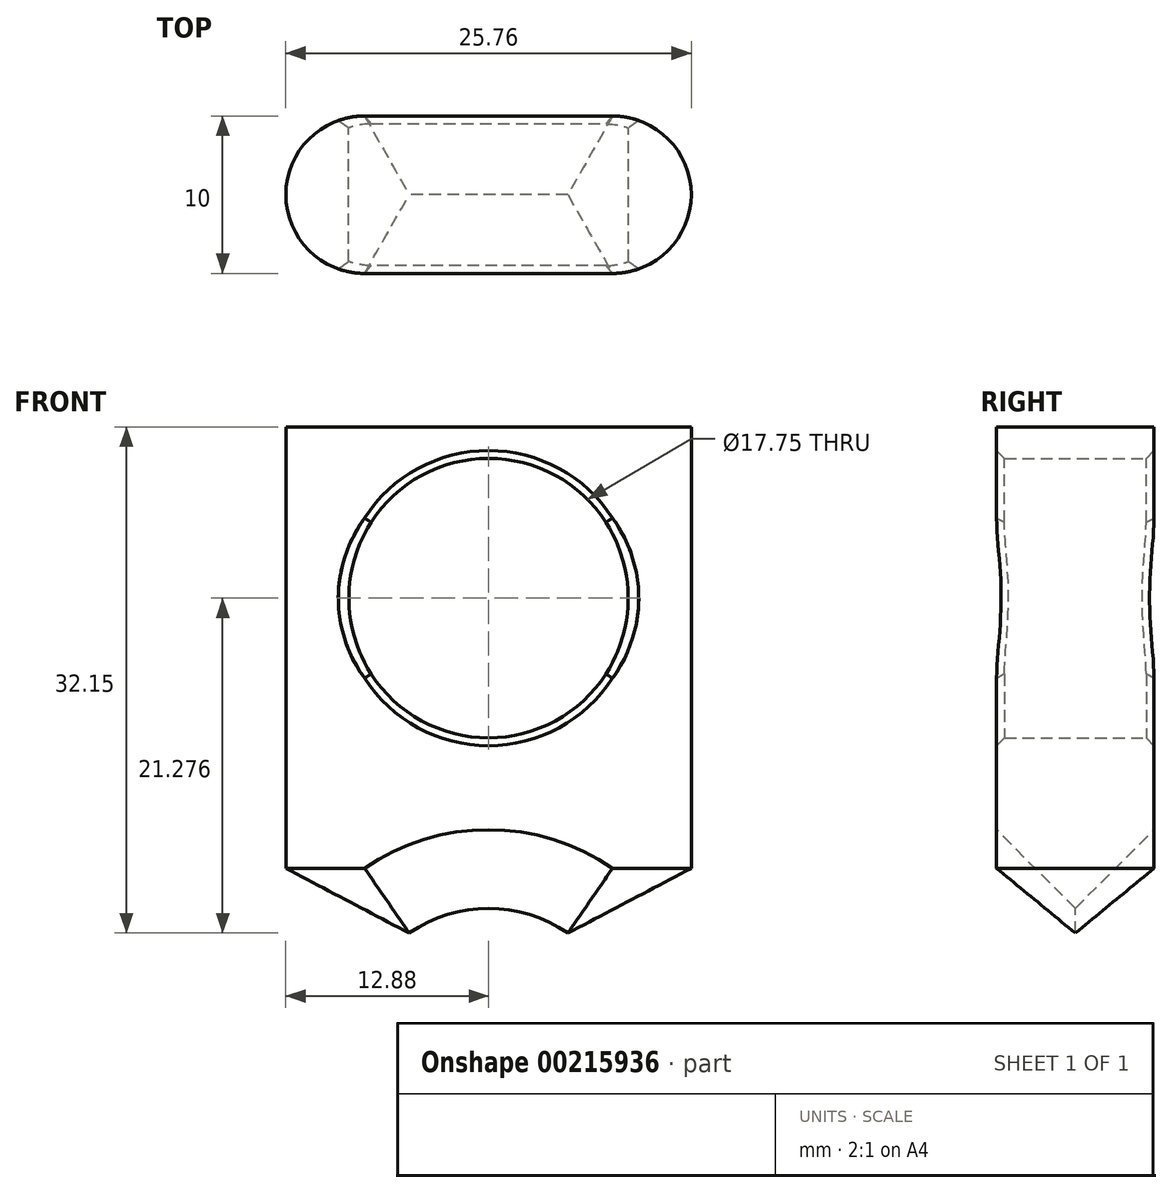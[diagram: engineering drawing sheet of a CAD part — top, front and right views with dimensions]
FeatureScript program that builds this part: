
annotation { "Feature Type Name" : "Feature", "Feature Type Description" : "" }
export const myFeature = defineFeature(function(context is Context, id is Id, definition is map)
    precondition{}
    {
        {
            var Q0;
            Q0=qCreatedBy(makeId("Front.planeOp"),FACE);
            var sketch = newSketch(context, id + "F0", { "sketchPlane" : qUnion([Q0])});
            skCircle(sketch, "E0", {"center": v(0, 0) * mm, "radius": 8.88 * mm});
            skLineSegment(sketch, "E1.bottom", {"start": v(-12.88, -10.54) * mm, "end": v(12.88, -10.54) * mm});
            skLineSegment(sketch, "E1.top", {"start": v(-12.88, 39.46) * mm, "end": v(12.87, 39.46) * mm});
            skLineSegment(sketch, "E1.left", {"start": v(-12.88, -10.54) * mm, "end": v(-12.88, 39.46) * mm});
            skLineSegment(sketch, "E1.right", {"start": v(12.88, -10.54) * mm, "end": v(12.87, 39.46) * mm});
            skCircle(sketch, "E2", {"center": v(0, 28.59) * mm, "radius": 8.88 * mm});
            skSolve(sketch);
        }
        {
            var Q0;
            Q0=makeQuery(id+"F0.imprint","IMPRINT",FACE,{"disambiguationData":[TD([[makeQuery(id+"F0.imprint","IMPRINT",EDGE,{"derivedFrom":sQuery(id+"F0.wireOp",EDGE,"E0")}),-1.0]])]});
            extrude(context, id + "F1", {"entities" : qUnion([Q0]), "depth" : 5 * mm, "hasSecondDirection" : true, "secondDirectionOppositeDirection" : true, "secondDirectionDepth" : 5 * mm});
        }
        {
            var Q0;
            Q0=makeQuery(id+"F1.opExtrude","CAP_EDGE",EDGE,{"disambiguationData":[OSD([sQuery(id+"F0.wireOp",EDGE,"E1.left")])],"isStart":false});
            var Q1;
            Q1=makeQuery(id+"F1.opExtrude","CAP_EDGE",EDGE,{"disambiguationData":[OSD([sQuery(id+"F0.wireOp",EDGE,"E1.left")])],"isStart":true});
            var Q2;
            Q2=makeQuery(id+"F1.opExtrude","CAP_EDGE",EDGE,{"disambiguationData":[OSD([sQuery(id+"F0.wireOp",EDGE,"E1.right")])],"isStart":false});
            var Q3;
            Q3=makeQuery(id+"F1.opExtrude","CAP_EDGE",EDGE,{"disambiguationData":[OSD([sQuery(id+"F0.wireOp",EDGE,"E1.right")])],"isStart":true});
            fillet(context, id + "F2", {"entities" : qUnion([Q0, Q1, Q2, Q3]), "radius" : 5 * mm, "tangentPropagation" : true, "allowEdgeOverflow" : false});
        }
        {
            var Q0;
            Q0=makeQuery(id+"F1.opExtrude","CAP_EDGE",EDGE,{"disambiguationData":[OSD([sQuery(id+"F0.wireOp",EDGE,"E0")])],"isStart":false});
            chamfer(context, id + "F3", {"entities" : qUnion([Q0]), "width" : 5 * mm, "tangentPropagation" : true});
        }
        {
            var Q0;
            Q0=makeQuery(id+"F0.imprint","IMPRINT",FACE,{"disambiguationData":[TD([[makeQuery(id+"F0.imprint","IMPRINT",EDGE,{"derivedFrom":sQuery(id+"F0.wireOp",EDGE,"E2")}),1.0]])]});
            extrude(context, id + "F4", {"entities" : qUnion([Q0]), "operationType" : NewBodyOperationType.REMOVE, "oppositeDirection" : true, "depth" : 25 * mm, "hasSecondDirection" : true, "secondDirectionOppositeDirection" : false, "secondDirectionDepth" : 25 * mm});
        }
        {
            var Q0;
            Q0=makeQuery(id+"F1.opExtrude","CAP_EDGE",EDGE,{"disambiguationData":[OSD([sQuery(id+"F0.wireOp",EDGE,"E2")])],"isStart":true});
            var Q1;
            Q1=makeQuery(id+"F1.opExtrude","CAP_EDGE",EDGE,{"disambiguationData":[OSD([sQuery(id+"F0.wireOp",EDGE,"E2")])],"isStart":false});
            chamfer(context, id + "F5", {"entities" : qUnion([Q0, Q1]), "width" : .5 * mm, "tangentPropagation" : true});
        }
    });
